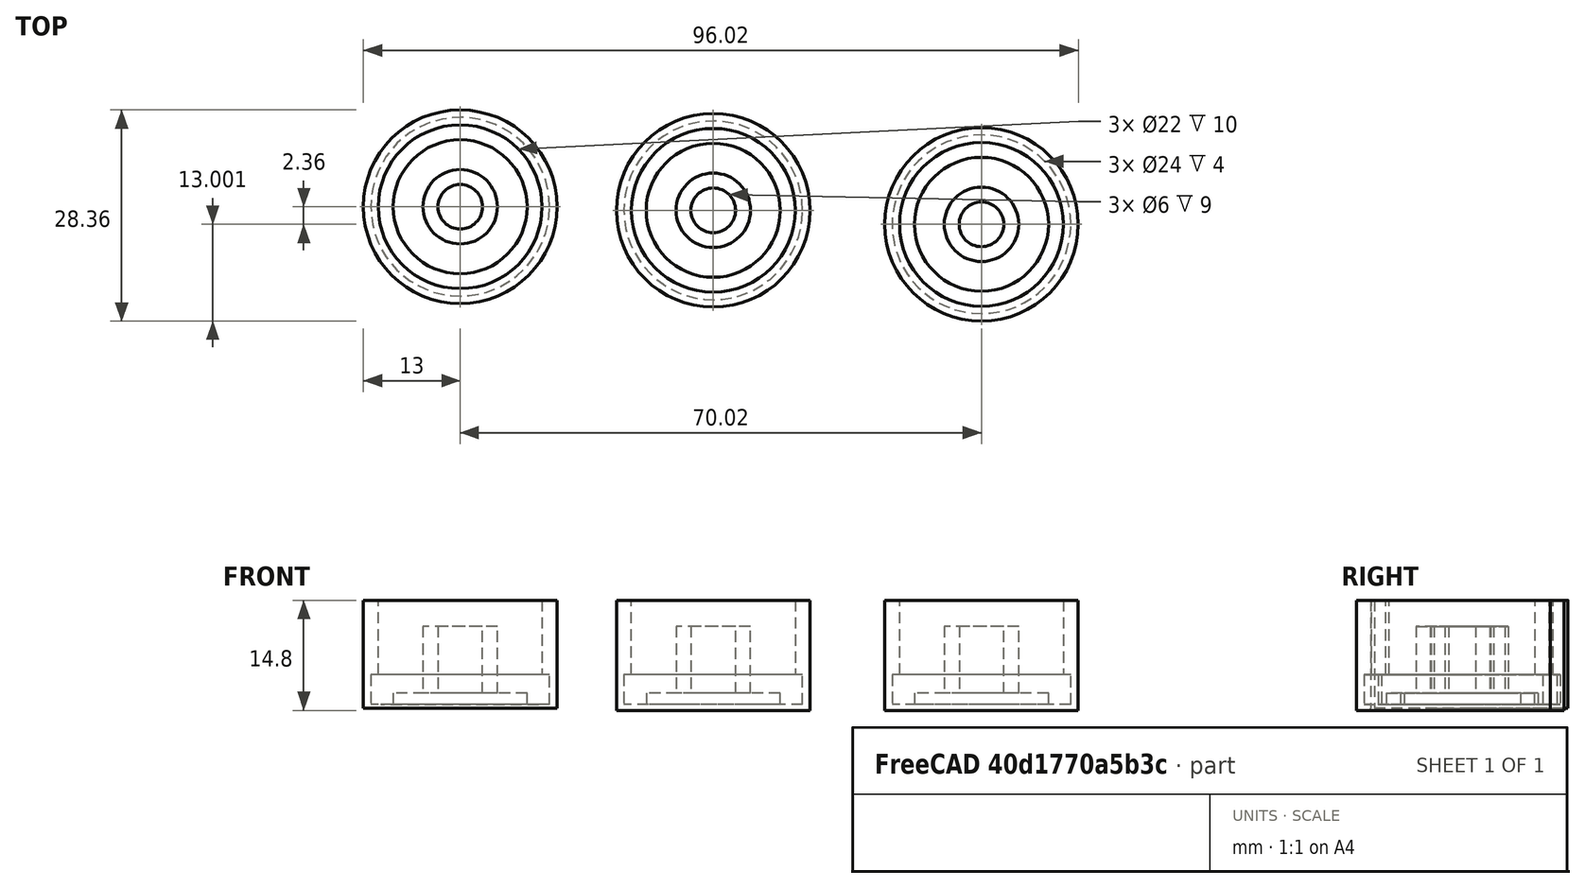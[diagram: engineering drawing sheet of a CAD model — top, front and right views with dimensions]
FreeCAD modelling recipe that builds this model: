
FCSTD DOCUMENT  (FreeCAD 0.18.3R)
Label: lamp.pot.button
License: All rights reserved
LicenseURL: http://en.wikipedia.org/wiki/All_rights_reserved
objects: Part::Extrusion×7, Part::Part2DObjectPython×6, Part::Cut×3, Part::MultiFuse×3, Part::Feature×3
note: 22 computed .brp shape members not serialized (recipe doc carries the construction recipe); baked Part::Feature solids carry a one-line shape summary decoded from their .brp

FEATURE [Part::Part2DObjectPython] Circle  # Draft 2D object (typed FeaturePython)
  FirstAngle = 0
  LastAngle = 0
  MakeFace = true
  Placement = pos=(17.628,9.63914,-0.734496) rot=(1,0,0;3.14159rad)
  Radius = 13
FEATURE [Part::Extrusion] Extrusion
  Base = -> Circle
  Dir = (0,0,14.5)
  DirMode = 0
  FaceMakerClass = Part::FaceMakerBullseye
  LengthFwd = 0
  LengthRev = 0
  Solid = true
  Symmetric = false
FEATURE [Part::Part2DObjectPython] Circle066  # Draft 2D object (typed FeaturePython)
  FirstAngle = 0
  LastAngle = 0
  MakeFace = true
  Placement = pos=(17.628,9.63914,13.7655) rot=(0,0,1;0rad)
  Radius = 11
FEATURE [Part::Extrusion] Extrusion012
  Base = -> Circle066
  Dir = (0,0,-14)
  DirMode = 0
  FaceMakerClass = Part::FaceMakerBullseye
  LengthFwd = 0
  LengthRev = 0
  Solid = true
  Symmetric = false
FEATURE [Part::Cut] Cut
  Base = -> Extrusion
  Placement = pos=(-75.7879,-6.24817,9.7345) rot=(0,0,1;0rad)
  Tool = -> Extrusion012
FEATURE [Part::Part2DObjectPython] Circle067  # Draft 2D object (typed FeaturePython)
  FirstAngle = 0
  LastAngle = 0
  MakeFace = true
  Placement = pos=(-58.1599,3.39097,9) rot=(1,0,0;3.14159rad)
  Radius = 3
FEATURE [Part::Part2DObjectPython] Circle068  # Draft 2D object (typed FeaturePython)
  FirstAngle = 0
  LastAngle = 0
  MakeFace = true
  Placement = pos=(-58.1599,3.39097,9) rot=(1,0,0;3.14159rad)
  Radius = 5
FEATURE [Part::Extrusion] Extrude
  Base = -> Circle067
  Dir = (0,0,-1)
  DirMode = 2
  FaceMakerClass = Part::FaceMakerBullseye
  LengthFwd = -11
  LengthRev = 0
  Solid = false
  Symmetric = false
FEATURE [Part::Extrusion] Extrude071
  Base = -> Circle068
  Dir = (0,0,-1)
  DirMode = 2
  FaceMakerClass = Part::FaceMakerBullseye
  LengthFwd = -11
  LengthRev = 0
  Solid = false
  Symmetric = false
FEATURE [Part::Cut] Cut047
  Base = -> Extrude071
  Tool = -> Extrude
FEATURE [Part::Part2DObjectPython] Circle069  # Draft 2D object (typed FeaturePython)
  FirstAngle = 0
  LastAngle = 0
  MakeFace = true
  Placement = pos=(-58.1599,3.39097,9) rot=(1,0,0;3.14159rad)
  Radius = 9
FEATURE [Part::Extrusion] Extrude072
  Base = -> Circle069
  Dir = (0,0,-1)
  DirMode = 2
  FaceMakerClass = Part::FaceMakerBullseye
  LengthFwd = -2
  LengthRev = 0
  Solid = false
  Symmetric = false
FEATURE [Part::MultiFuse] Fusion
  Shapes = -> [Cut047,Extrude072]
FEATURE [Part::Part2DObjectPython] Circle070  # Draft 2D object (typed FeaturePython)
  FirstAngle = 0
  LastAngle = 0
  MakeFace = true
  Placement = pos=(-85.1183,-1.00804,9) rot=(0,0,1;0rad)
  Radius = 12
FEATURE [Part::Extrusion] Extrusion013
  Base = -> Circle070
  Dir = (0,0,4)
  DirMode = 0
  FaceMakerClass = Part::FaceMakerBullseye
  LengthFwd = 0
  LengthRev = 0
  Placement = pos=(26.9583,4.39901,0.5) rot=(0,0,1;0rad)
  Solid = true
  Symmetric = false
FEATURE [Part::Cut] Cut048
  Base = -> Cut
  Tool = -> Extrusion013
FEATURE [Part::MultiFuse] Fusion001
  Shapes = -> [Fusion,Cut048]
FEATURE [Part::Feature] Fusion001_solid001  label="Fusion001 (Solid)001"
  shape: bbox 26 x 26 x 14.5 mm, 13 faces (baked)
FEATURE [Part::Feature] Face
  shape: bbox 26 x 26 x 2e-07 mm, 1 faces, 0 solids (baked)
FEATURE [Part::Extrusion] Extrusion014
  Base = -> Face
  Dir = (0,0,-0.3)
  DirMode = 0
  FaceMakerClass = Part::FaceMakerBullseye
  LengthFwd = 0
  LengthRev = 0
  Solid = true
  Symmetric = false
FEATURE [Part::MultiFuse] Fusion002
  Placement = pos=(0,15.2634,-6.7e-15) rot=(0,0,1;0rad)
  Shapes = -> [Fusion001_solid001,Extrusion014]
FEATURE [Part::Feature] Fusion002_solid001  label="Fusion002 (Solid)001"
  Placement = pos=(36.0317,13.3868,-5.8e-15) rot=(0,0,1;0rad)
  shape: bbox 26 x 26 x 14.8 mm, 13 faces (baked)
